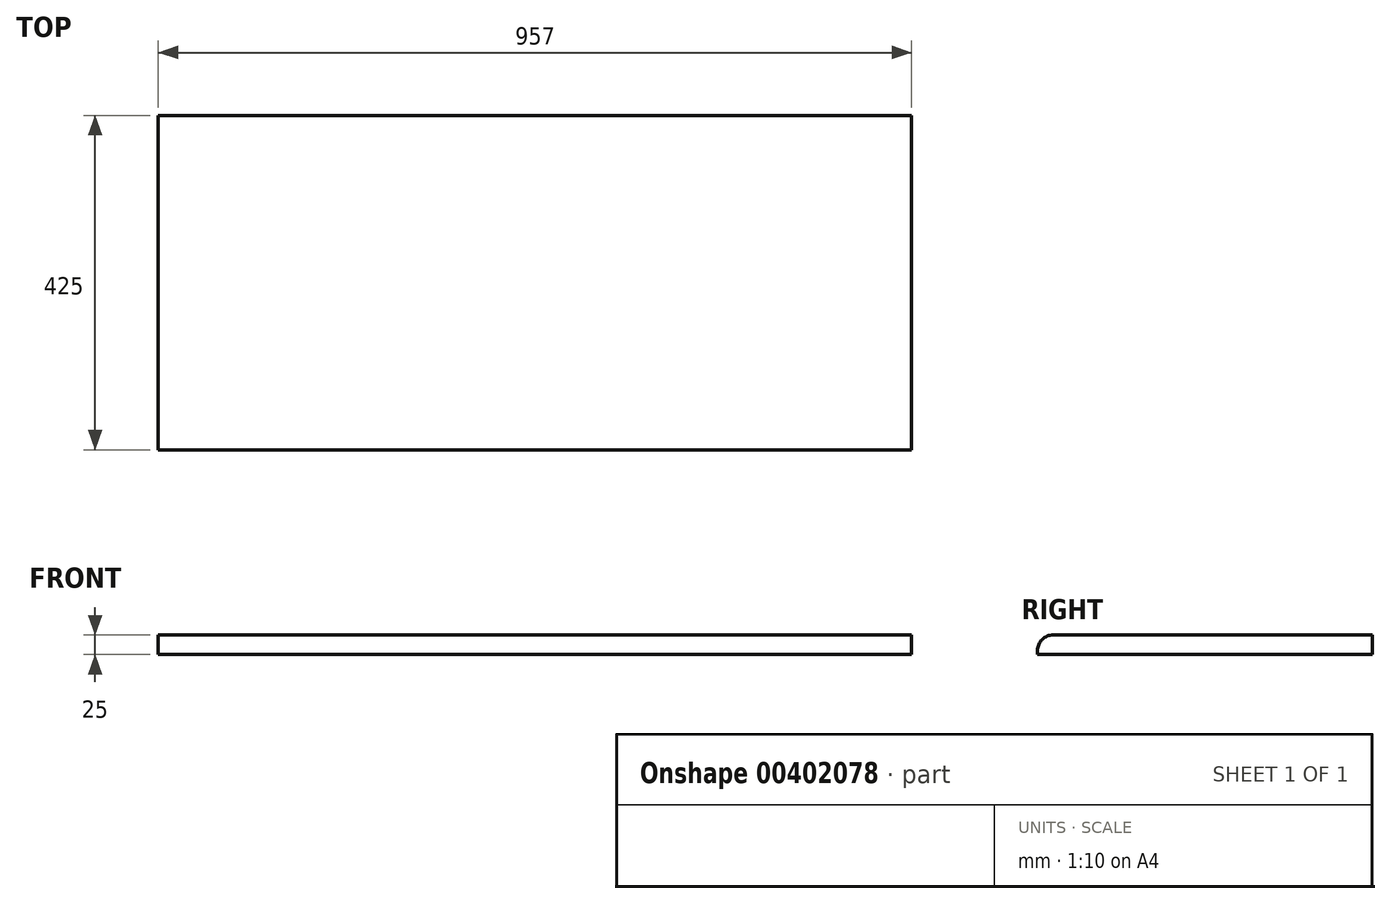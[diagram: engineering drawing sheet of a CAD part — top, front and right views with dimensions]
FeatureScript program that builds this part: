
annotation { "Feature Type Name" : "Feature", "Feature Type Description" : "" }
export const myFeature = defineFeature(function(context is Context, id is Id, definition is map)
    precondition{}
    {
        {
            var Q0;
            Q0=qCreatedBy(makeId("Top.planeOp"),FACE);
            var sketch = newSketch(context, id + "F0", { "sketchPlane" : qUnion([Q0])});
            skLineSegment(sketch, "E0.bottom", {"start": v(0, 0) * mm, "end": v(957, 0) * mm});
            skLineSegment(sketch, "E0.top", {"start": v(0, 425) * mm, "end": v(957, 425) * mm});
            skLineSegment(sketch, "E0.left", {"start": v(0, 0) * mm, "end": v(0, 425) * mm});
            skLineSegment(sketch, "E0.right", {"start": v(957, 0) * mm, "end": v(957, 425) * mm});
            skSolve(sketch);
        }
        {
            var Q0;
            Q0=qSketchRegion(id+"F0",true);
            extrude(context, id + "F1", {"entities" : qUnion([Q0]), "depth" : 25 * mm});
        }
        {
            var Q0;
            Q0=makeQuery(id+"F1.opExtrude","CAP_EDGE",EDGE,{"disambiguationData":[OSD([sQuery(id+"F0.wireOp",EDGE,"E0.bottom")])],"isStart":false});
            fillet(context, id + "F2", {"entities" : qUnion([Q0]), "radius" : 20 * mm, "tangentPropagation" : true, "allowEdgeOverflow" : false});
        }
    });
